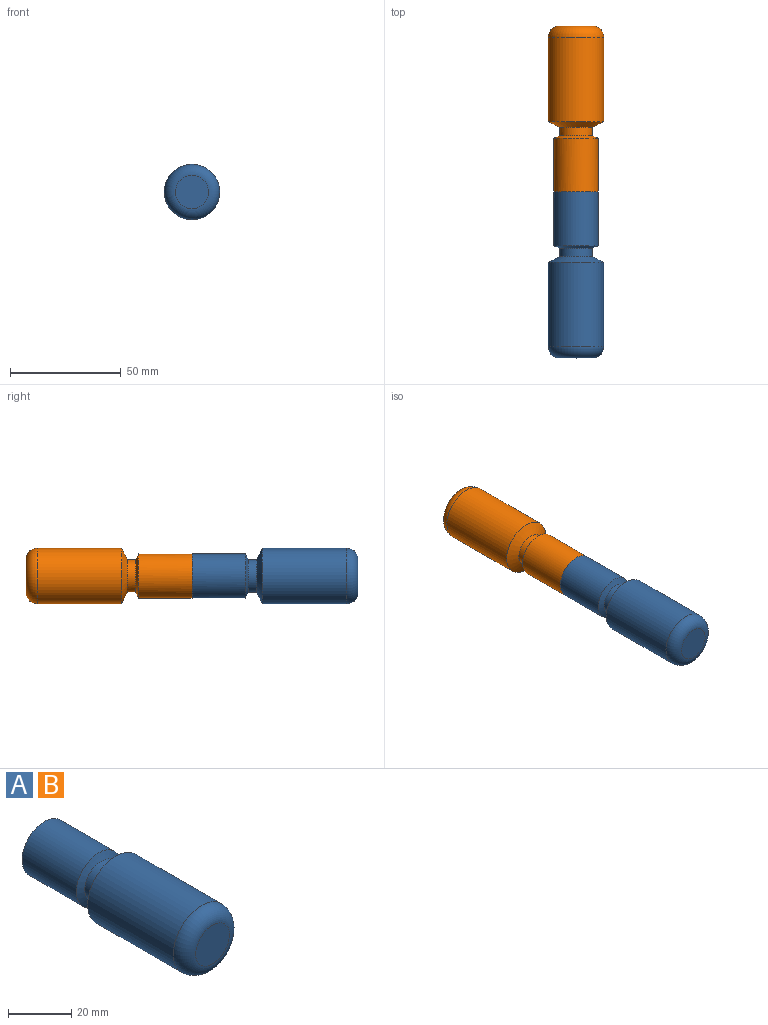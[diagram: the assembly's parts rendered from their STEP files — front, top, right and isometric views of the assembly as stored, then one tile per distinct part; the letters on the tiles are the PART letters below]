
ASSEMBLY  parts=2 mates=2
PART A: 10 faces, bbox 27.1x75x27.1 mm
  f0: cylinder r=10mm len=24.21mm, axis (0,1,0), area 1521mm2, adj f1,f4
  f1: plane 20x20mm, normal (0,1,0), area 285.9mm2, adj f0,f3
  f2: cone r=0mm half-angle=59deg, axis (0,1,0), area 33mm2, adj f3
  f3: cylinder r=3mm len=17.2mm, axis (0,1,0), area 324.2mm2, adj f1,f2
  f4: cone r=7.37mm half-angle=66.1deg, axis (0,1,0), area 156.9mm2, adj f0,f6
  f5: cone r=13.48mm half-angle=62.7deg, axis (0,-1,0), area 360.2mm2, adj f6,f9
  f6: cylinder r=7.37mm len=14.74mm, axis (0,-1,0), area 175.1mm2, adj f4,f5
  f7: plane 15x15mm, normal (0,-1,0), area 176.7mm2, adj f8
  f8: torus R=7.5mm, axis (0,-1,0), area 527.2mm2, adj f7,f9
  f9: cylinder r=12.5mm len=38.2mm, axis (0,1,0), area 3000.5mm2, adj f5,f8
PART B: same geometry as A
PLACE A t=(-91.55,4.52,-30.52)mm
PLACE B rot(axis=(1,0,0),180deg) t=(-91.55,4.52,-30.52)mm
MATE planar B.f0 <-> A.f0  axis (0,-1,0) through (-91.55,4.52,-30.52)mm
MATE cylindrical B.f0 <-> A.f0  axis (0,-1,0) through (-91.55,4.52,-30.52)mm
